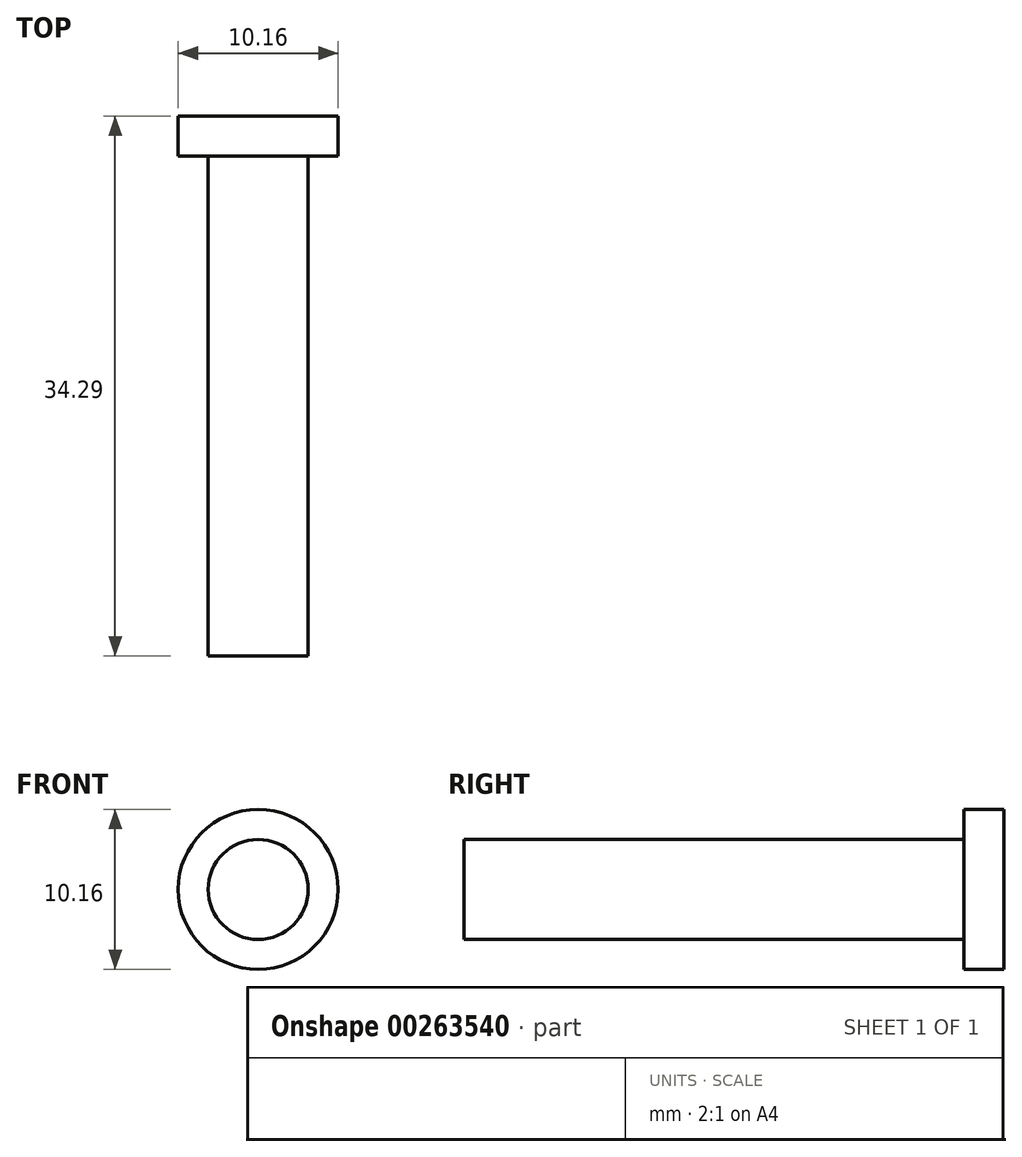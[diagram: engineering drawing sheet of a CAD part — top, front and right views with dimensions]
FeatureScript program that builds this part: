
annotation { "Feature Type Name" : "Feature", "Feature Type Description" : "" }
export const myFeature = defineFeature(function(context is Context, id is Id, definition is map)
    precondition{}
    {
        {
            var Q0;
            Q0=qCreatedBy(makeId("Front.planeOp"),FACE);
            var sketch = newSketch(context, id + "F0", { "sketchPlane" : qUnion([Q0])});
            skCircle(sketch, "E0", {"center": v(0, 0) * mm, "radius": 5.08 * mm});
            skCircle(sketch, "E1", {"center": v(0, 0) * mm, "radius": 3.18 * mm});
            skSolve(sketch);
        }
        {
            var Q0;
            Q0=makeQuery(id+"F0.imprint","IMPRINT",FACE,{"disambiguationData":[TD([[makeQuery(id+"F0.imprint","IMPRINT",EDGE,{"derivedFrom":sQuery(id+"F0.wireOp",EDGE,"E1")}),1.0]])]});
            extrude(context, id + "F1", {"entities" : qUnion([Q0]), "depth" : 34.3 * mm});
        }
        {
            var Q0;
            Q0=makeQuery(id+"F0.imprint","IMPRINT",FACE,{"disambiguationData":[TD([[makeQuery(id+"F0.imprint","IMPRINT",EDGE,{"derivedFrom":sQuery(id+"F0.wireOp",EDGE,"E0")}),1.0]])]});
            var Q1;
            Q1=sQuery(id+"F0.wireOp",EDGE,"E0");
            extrude(context, id + "F2", {"entities" : qUnion([Q0]), "operationType" : NewBodyOperationType.ADD, "surfaceEntities" : qUnion([Q1]), "depth" : 2.54 * mm});
        }
    });
